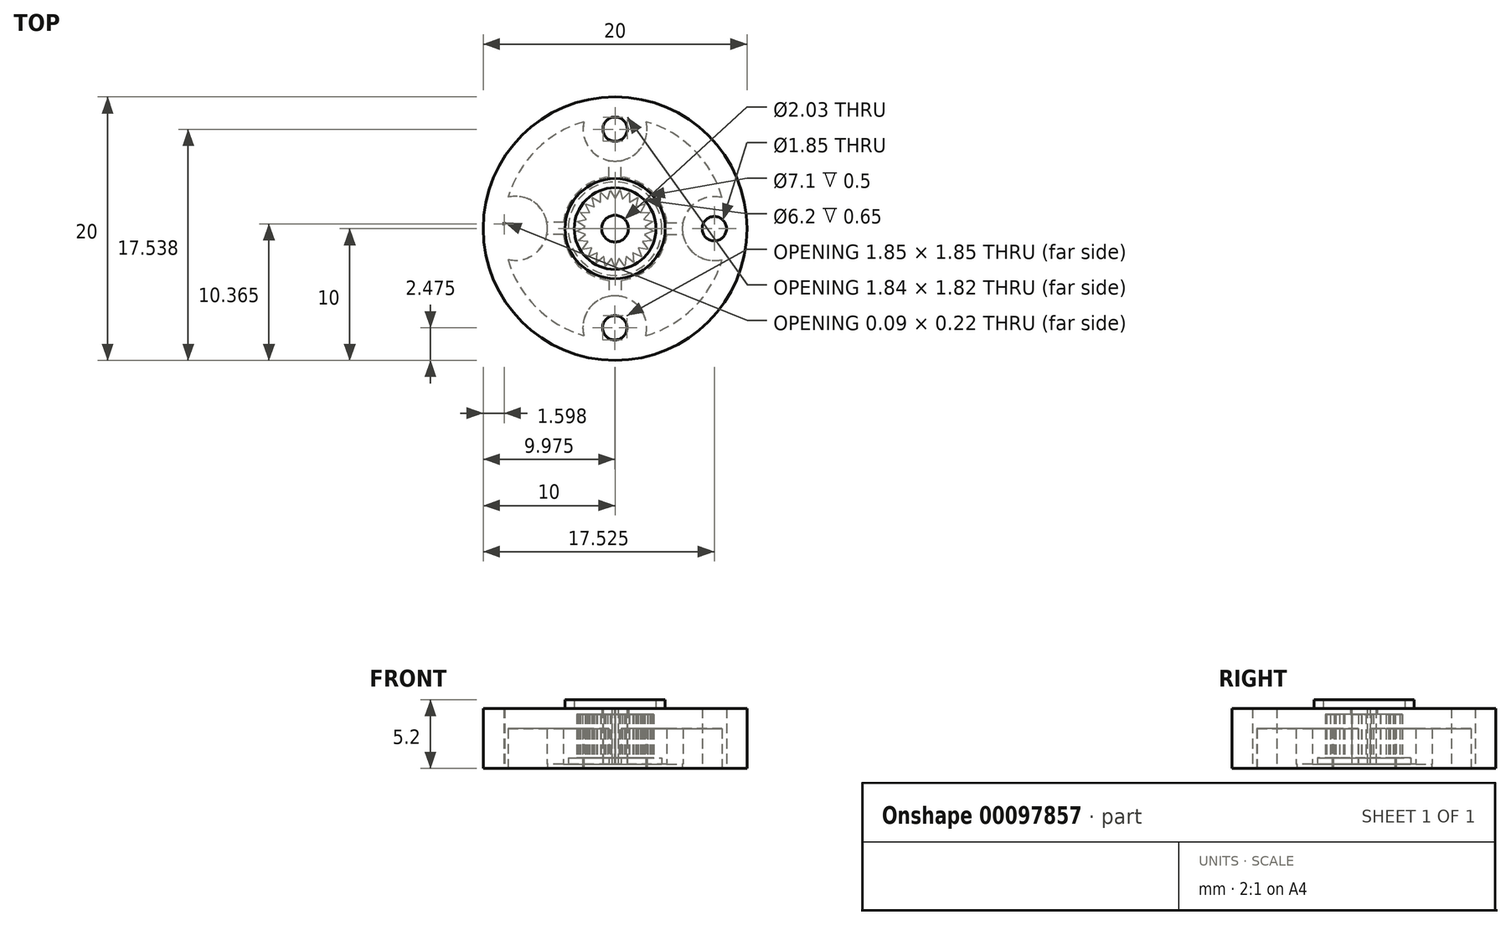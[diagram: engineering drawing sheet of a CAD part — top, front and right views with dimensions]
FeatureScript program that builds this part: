
annotation { "Feature Type Name" : "Feature", "Feature Type Description" : "" }
export const myFeature = defineFeature(function(context is Context, id is Id, definition is map)
    precondition{}
    {
        {
            var Q0;
            Q0=qCreatedBy(makeId("Top.planeOp"),FACE);
            var sketch = newSketch(context, id + "F0", { "sketchPlane" : qUnion([Q0])});
            skCircle(sketch, "E0", {"center": v(0, 0) * mm, "radius": 10 * mm});
            skSolve(sketch);
        }
        {
            var Q0;
            Q0=qSketchRegion(id+"F0",true);
            extrude(context, id + "F1", {"entities" : qUnion([Q0]), "depth" : 4.55 * mm});
        }
        {
            var Q0;
            Q0=makeQuery(id+"F1.opExtrude","CAP_FACE",FACE,{"disambiguationData":[OSD([sQuery(id+"F0.wireOp",EDGE,"E0")])],"isStart":true});
            var sketch = newSketch(context, id + "F2", { "sketchPlane" : qUnion([Q0])});
            skCircle(sketch, "E1", {"center": v(0, 0) * mm, "radius": 8.45 * mm});
            skCircle(sketch, "E2", {"center": v(0, 0) * mm, "radius": 3.95 * mm});
            skCircle(sketch, "E3", {"center": v(0, 0) * mm, "radius": 3.55 * mm});
            skLineSegment(sketch, "E4", {"start": v(0, 8.45) * mm, "end": v(0, -8.45) * mm, "construction": true});
            skLineSegment(sketch, "E5", {"start": v(8.45, 0) * mm, "end": v(-8.45, 0) * mm, "construction": true});
            skLineSegment(sketch, "E6", {"start": v(0.45, 3.92) * mm, "end": v(0.45, 5.15) * mm});
            skLineSegment(sketch, "E7", {"start": v(-0.45, 3.92) * mm, "end": v(-0.45, 5.14) * mm});
            skLineSegment(sketch, "E8", {"start": v(3.92, 0.45) * mm, "end": v(5.14, 0.45) * mm});
            skLineSegment(sketch, "E9", {"start": v(3.92, -0.45) * mm, "end": v(5.14, -0.45) * mm});
            skLineSegment(sketch, "E10", {"start": v(0.45, -3.92) * mm, "end": v(0.45, -5.17) * mm});
            skLineSegment(sketch, "E11", {"start": v(-0.45, -3.92) * mm, "end": v(-0.45, -5.17) * mm});
            skLineSegment(sketch, "E12", {"start": v(-3.92, -0.47) * mm, "end": v(-5.17, -0.47) * mm});
            skLineSegment(sketch, "E13", {"start": v(-3.93, 0.43) * mm, "end": v(-5.17, 0.43) * mm});
            skCircle(sketch, "E14", {"center": v(7.52, 0) * mm, "radius": 0.93 * mm});
            skCircle(sketch, "E15", {"center": v(7.52, 0) * mm, "radius": 2.43 * mm});
            skCircle(sketch, "E16.1.0", {"center": v(-0.02, 7.53) * mm, "radius": 0.93 * mm});
            skCircle(sketch, "E16.1.1", {"center": v(-0.02, 7.53) * mm, "radius": 2.43 * mm});
            skCircle(sketch, "E16.2.0", {"center": v(-7.55, -0.02) * mm, "radius": 0.93 * mm});
            skCircle(sketch, "E16.2.1", {"center": v(-7.55, -0.02) * mm, "radius": 2.43 * mm});
            skCircle(sketch, "E16.3.0", {"center": v(0, -7.55) * mm, "radius": 0.93 * mm});
            skCircle(sketch, "E16.3.1", {"center": v(0, -7.55) * mm, "radius": 2.43 * mm});
            skPoint(sketch, "E16.center", {"position": v(-0.01, -0.01) * mm});
            skLineSegment(sketch, "E17.trimOffspring", {"start": v(8.33, -0.45) * mm, "end": v(8.44, -0.45) * mm});
            skLineSegment(sketch, "E18.trimOffspring", {"start": v(8.33, 0.45) * mm, "end": v(8.44, 0.45) * mm});
            skLineSegment(sketch, "E19.trimOffspring", {"start": v(-0.45, -8.36) * mm, "end": v(-0.45, -8.44) * mm});
            skLineSegment(sketch, "E20.trimOffspring", {"start": v(0.45, -8.36) * mm, "end": v(0.45, -8.44) * mm});
            skLineSegment(sketch, "E21.trimOffspring", {"start": v(-8.36, -0.47) * mm, "end": v(-8.44, -0.47) * mm});
            skLineSegment(sketch, "E22.trimOffspring", {"start": v(-8.36, 0.43) * mm, "end": v(-8.44, 0.43) * mm});
            skLineSegment(sketch, "E23.trimOffspring", {"start": v(-0.45, 8.35) * mm, "end": v(-0.45, 8.44) * mm});
            skLineSegment(sketch, "E24.trimOffspring", {"start": v(0.45, 8.32) * mm, "end": v(0.45, 8.44) * mm});
            skCircle(sketch, "E25", {"center": v(0, 0) * mm, "radius": 1.02 * mm});
            skSolve(sketch);
        }
        {
            var Q0;
            {var subQ1=sQuery(id+"F2.wireOp",EDGE,"E9");Q0=makeQuery(id+"F2.imprint","IMPRINT",FACE,{"disambiguationData":[TD([[makeQuery(id+"F2.imprint","IMPRINT",EDGE,{"derivedFrom":subQ1}),-1.0]])]});}
            var Q1;
            {var subQ0=sQuery(id+"F2.wireOp",EDGE,"E11");Q1=makeQuery(id+"F2.imprint","IMPRINT",FACE,{"disambiguationData":[TD([[makeQuery(id+"F2.imprint","IMPRINT",EDGE,{"derivedFrom":subQ0}),-1.0]])]});}
            var Q2;
            {var subQ0=sQuery(id+"F2.wireOp",EDGE,"E14");var subQ1=makeQuery(id+"F2.imprint","INTERSECT",VERTEX,{"derivedFrom":[subQ0,sQuery(id+"F2.wireOp",EDGE,"E18.trimOffspring")]});Q2=makeQuery(id+"F2.imprint","IMPRINT",FACE,{"disambiguationData":[TD([[makeQuery(id+"F2.imprint","IMPRINT",EDGE,{"disambiguationData":[TD([[subQ1,1.0]])],"derivedFrom":subQ0}),1.0]])]});}
            var Q3;
            {var subQ0=sQuery(id+"F2.wireOp",EDGE,"E16.3.0");var subQ1=sQuery(id+"F2.wireOp",EDGE,"E1");var subQ2=makeQuery(id+"F2.imprint","INTERSECT",VERTEX,{"disambiguationData":[OD(0.0)],"derivedFrom":[subQ1,subQ0]});Q3=makeQuery(id+"F2.imprint","IMPRINT",FACE,{"disambiguationData":[TD([[makeQuery(id+"F2.imprint","IMPRINT",EDGE,{"disambiguationData":[TD([[subQ2,-1.0]])],"derivedFrom":subQ1}),1.0]])]});}
            var Q4;
            {var subQ0=sQuery(id+"F2.wireOp",EDGE,"E16.2.0");var subQ1=sQuery(id+"F2.wireOp",EDGE,"E1");var subQ2=makeQuery(id+"F2.imprint","INTERSECT",VERTEX,{"disambiguationData":[OD(0.0)],"derivedFrom":[subQ1,subQ0]});Q4=makeQuery(id+"F2.imprint","IMPRINT",FACE,{"disambiguationData":[TD([[makeQuery(id+"F2.imprint","IMPRINT",EDGE,{"disambiguationData":[TD([[subQ2,-1.0]])],"derivedFrom":subQ1}),1.0]])]});}
            var Q5;
            {var subQ0=sQuery(id+"F2.wireOp",EDGE,"E7");Q5=makeQuery(id+"F2.imprint","IMPRINT",FACE,{"disambiguationData":[TD([[makeQuery(id+"F2.imprint","IMPRINT",EDGE,{"derivedFrom":subQ0}),1.0]])]});}
            var Q6;
            {var subQ0=sQuery(id+"F2.wireOp",EDGE,"E6");Q6=makeQuery(id+"F2.imprint","IMPRINT",FACE,{"disambiguationData":[TD([[makeQuery(id+"F2.imprint","IMPRINT",EDGE,{"derivedFrom":subQ0}),-1.0]])]});}
            var Q7;
            Q7=makeQuery(id+"F2.imprint","IMPRINT",FACE,{"disambiguationData":[TD([[makeQuery(id+"F2.imprint","IMPRINT",EDGE,{"derivedFrom":sQuery(id+"F2.wireOp",EDGE,"E25")}),1.0]])]});
            var Q8;
            {var subQ0=sQuery(id+"F2.wireOp",EDGE,"E16.1.0");var subQ1=makeQuery(id+"F2.imprint","INTERSECT",VERTEX,{"derivedFrom":[subQ0,sQuery(id+"F2.wireOp",EDGE,"E23.trimOffspring")]});Q8=makeQuery(id+"F2.imprint","IMPRINT",FACE,{"disambiguationData":[TD([[makeQuery(id+"F2.imprint","IMPRINT",EDGE,{"disambiguationData":[TD([[subQ1,-1.0]])],"derivedFrom":subQ0}),1.0]])]});}
            extrude(context, id + "F3", {"entities" : qUnion([Q0, Q1, Q2, Q3, Q4, Q5, Q6, Q7, Q8]), "operationType" : NewBodyOperationType.REMOVE, "oppositeDirection" : true, "depth" : 3 * mm});
        }
        {
            var Q0;
            {var subQ0=sQuery(id+"F2.wireOp",EDGE,"E6");Q0=makeQuery(id+"F2.imprint","IMPRINT",FACE,{"disambiguationData":[TD([[makeQuery(id+"F2.imprint","IMPRINT",EDGE,{"derivedFrom":subQ0}),1.0]])]});}
            var Q1;
            {var subQ0=sQuery(id+"F2.wireOp",EDGE,"E8");Q1=makeQuery(id+"F2.imprint","IMPRINT",FACE,{"disambiguationData":[TD([[makeQuery(id+"F2.imprint","IMPRINT",EDGE,{"derivedFrom":subQ0}),-1.0]])]});}
            var Q2;
            {var subQ0=sQuery(id+"F2.wireOp",EDGE,"E10");Q2=makeQuery(id+"F2.imprint","IMPRINT",FACE,{"disambiguationData":[TD([[makeQuery(id+"F2.imprint","IMPRINT",EDGE,{"derivedFrom":subQ0}),-1.0]])]});}
            var Q3;
            {var subQ0=sQuery(id+"F2.wireOp",EDGE,"E12");Q3=makeQuery(id+"F2.imprint","IMPRINT",FACE,{"disambiguationData":[TD([[makeQuery(id+"F2.imprint","IMPRINT",EDGE,{"derivedFrom":subQ0}),-1.0]])]});}
            var Q4;
            Q4=makeQuery(id+"F2.imprint","IMPRINT",FACE,{"disambiguationData":[TD([[makeQuery(id+"F2.imprint","IMPRINT",EDGE,{"derivedFrom":sQuery(id+"F2.wireOp",EDGE,"E3")}),-1.0]])]});
            extrude(context, id + "F4", {"entities" : qUnion([Q0, Q1, Q2, Q3, Q4]), "operationType" : NewBodyOperationType.REMOVE, "oppositeDirection" : true, "depth" : .3 * mm});
        }
        {
            var Q0;
            Q0=makeQuery(id+"F2.imprint","IMPRINT",FACE,{"disambiguationData":[TD([[makeQuery(id+"F2.imprint","IMPRINT",EDGE,{"derivedFrom":sQuery(id+"F2.wireOp",EDGE,"E3")}),1.0]])]});
            extrude(context, id + "F5", {"entities" : qUnion([Q0]), "operationType" : NewBodyOperationType.REMOVE, "oppositeDirection" : true, "depth" : .8 * mm});
        }
        {
            var Q0;
            Q0=makeQuery(id+"F3.boolean.opBoolean","COPY",FACE,{"derivedFrom":makeQuery(id+"F3.opExtrude","CAP_FACE",FACE,{"disambiguationData":[OSD([sQuery(id+"F2.wireOp",EDGE,"E16.1.0")])],"isStart":false})});
            var Q1;
            Q1=makeQuery(id+"F3.boolean.opBoolean","COPY",FACE,{"derivedFrom":makeQuery(id+"F3.opExtrude","CAP_FACE",FACE,{"disambiguationData":[OSD([sQuery(id+"F2.wireOp",EDGE,"E14")])],"isStart":false})});
            var Q2;
            Q2=makeQuery(id+"F3.boolean.opBoolean","COPY",FACE,{"derivedFrom":makeQuery(id+"F3.opExtrude","CAP_FACE",FACE,{"disambiguationData":[OSD([sQuery(id+"F2.wireOp",EDGE,"E1"),sQuery(id+"F2.wireOp",EDGE,"E16.3.0")])],"isStart":false})});
            var Q3;
            Q3=makeQuery(id+"F3.boolean.opBoolean","COPY",FACE,{"derivedFrom":makeQuery(id+"F3.opExtrude","CAP_FACE",FACE,{"disambiguationData":[OSD([sQuery(id+"F2.wireOp",EDGE,"E25")])],"isStart":false})});
            var Q4;
            Q4=makeQuery(id+"F3.boolean.opBoolean","COPY",FACE,{"derivedFrom":makeQuery(id+"F3.opExtrude","CAP_FACE",FACE,{"disambiguationData":[OSD([sQuery(id+"F2.wireOp",EDGE,"E1"),sQuery(id+"F2.wireOp",EDGE,"E16.2.0")])],"isStart":false})});
            extrude(context, id + "F6", {"entities" : qUnion([Q0, Q1, Q2, Q3, Q4]), "operationType" : NewBodyOperationType.REMOVE, "oppositeDirection" : true, "depth" : 25 * mm});
        }
        {
            var Q0;
            Q0=makeQuery(id+"F5.boolean.opBoolean","COPY",FACE,{"derivedFrom":makeQuery(id+"F5.opExtrude","CAP_FACE",FACE,{"disambiguationData":[OSD([sQuery(id+"F2.wireOp",EDGE,"E3"),sQuery(id+"F2.wireOp",EDGE,"E25")])],"isStart":false})});
            var sketch = newSketch(context, id + "F7", { "sketchPlane" : qUnion([Q0])});
            skCircle(sketch, "E26", {"center": v(0, 0) * mm, "radius": 2.92 * mm});
            skLineSegment(sketch, "E27", {"start": v(0, -2.92) * mm, "end": v(0, 2.92) * mm, "construction": true});
            skCircle(sketch, "E28.cCircle", {"center": v(0, -2.7) * mm, "radius": 0.2 * mm});
            skLineSegment(sketch, "E28.0", {"start": v(-0.36, -2.9) * mm, "end": v(0, -2.28) * mm});
            skLineSegment(sketch, "E28.1", {"start": v(0, -2.28) * mm, "end": v(0.36, -2.9) * mm});
            skLineSegment(sketch, "E28.2", {"start": v(0.36, -2.9) * mm, "end": v(-0.36, -2.9) * mm});
            skPoint(sketch, "E28.0.midPoint", {"position": v(-0.18, -2.6) * mm});
            skLineSegment(sketch, "E29.1.0", {"start": v(0.38, -2.9) * mm, "end": v(0.57, -2.21) * mm});
            skLineSegment(sketch, "E29.1.1", {"start": v(0.57, -2.21) * mm, "end": v(1.07, -2.72) * mm});
            skLineSegment(sketch, "E29.1.2", {"start": v(1.07, -2.72) * mm, "end": v(0.38, -2.9) * mm});
            skLineSegment(sketch, "E29.2.0", {"start": v(1.09, -2.71) * mm, "end": v(1.1, -2) * mm});
            skLineSegment(sketch, "E29.2.1", {"start": v(1.1, -2) * mm, "end": v(1.7, -2.37) * mm});
            skLineSegment(sketch, "E29.2.2", {"start": v(1.7, -2.37) * mm, "end": v(1.09, -2.71) * mm});
            skLineSegment(sketch, "E29.3.0", {"start": v(1.73, -2.36) * mm, "end": v(1.56, -1.66) * mm});
            skLineSegment(sketch, "E29.3.1", {"start": v(1.56, -1.66) * mm, "end": v(2.24, -1.87) * mm});
            skLineSegment(sketch, "E29.3.2", {"start": v(2.24, -1.87) * mm, "end": v(1.73, -2.36) * mm});
            skLineSegment(sketch, "E29.4.0", {"start": v(2.26, -1.85) * mm, "end": v(1.93, -1.22) * mm});
            skLineSegment(sketch, "E29.4.1", {"start": v(1.93, -1.22) * mm, "end": v(2.64, -1.25) * mm});
            skLineSegment(sketch, "E29.4.2", {"start": v(2.64, -1.25) * mm, "end": v(2.26, -1.85) * mm});
            skLineSegment(sketch, "E29.5.0", {"start": v(2.65, -1.23) * mm, "end": v(2.17, -0.7) * mm});
            skLineSegment(sketch, "E29.5.1", {"start": v(2.17, -0.7) * mm, "end": v(2.87, -0.56) * mm});
            skLineSegment(sketch, "E29.5.2", {"start": v(2.87, -0.56) * mm, "end": v(2.65, -1.23) * mm});
            skLineSegment(sketch, "E29.6.0", {"start": v(2.87, -0.54) * mm, "end": v(2.28, -0.14) * mm});
            skLineSegment(sketch, "E29.6.1", {"start": v(2.28, -0.14) * mm, "end": v(2.92, 0.17) * mm});
            skLineSegment(sketch, "E29.6.2", {"start": v(2.92, 0.17) * mm, "end": v(2.87, -0.54) * mm});
            skLineSegment(sketch, "E29.7.0", {"start": v(2.91, 0.2) * mm, "end": v(2.24, 0.43) * mm});
            skLineSegment(sketch, "E29.7.1", {"start": v(2.24, 0.43) * mm, "end": v(2.78, 0.9) * mm});
            skLineSegment(sketch, "E29.7.2", {"start": v(2.78, 0.9) * mm, "end": v(2.91, 0.2) * mm});
            skLineSegment(sketch, "E29.8.0", {"start": v(2.77, 0.91) * mm, "end": v(2.07, 0.97) * mm});
            skLineSegment(sketch, "E29.8.1", {"start": v(2.07, 0.97) * mm, "end": v(2.47, 1.56) * mm});
            skLineSegment(sketch, "E29.8.2", {"start": v(2.47, 1.56) * mm, "end": v(2.77, 0.91) * mm});
            skLineSegment(sketch, "E29.9.0", {"start": v(2.46, 1.57) * mm, "end": v(1.76, 1.46) * mm});
            skLineSegment(sketch, "E29.9.1", {"start": v(1.76, 1.46) * mm, "end": v(2, 2.12) * mm});
            skLineSegment(sketch, "E29.9.2", {"start": v(2, 2.12) * mm, "end": v(2.46, 1.57) * mm});
            skLineSegment(sketch, "E29.10.0", {"start": v(2, 2.14) * mm, "end": v(1.34, 1.85) * mm});
            skLineSegment(sketch, "E29.10.1", {"start": v(1.34, 1.85) * mm, "end": v(1.42, 2.55) * mm});
            skLineSegment(sketch, "E29.10.2", {"start": v(1.42, 2.55) * mm, "end": v(2, 2.14) * mm});
            skLineSegment(sketch, "E29.11.0", {"start": v(1.4, 2.56) * mm, "end": v(0.84, 2.12) * mm});
            skLineSegment(sketch, "E29.11.1", {"start": v(0.84, 2.12) * mm, "end": v(0.74, 2.83) * mm});
            skLineSegment(sketch, "E29.11.2", {"start": v(0.74, 2.83) * mm, "end": v(1.4, 2.56) * mm});
            skLineSegment(sketch, "E29.12.0", {"start": v(0.72, 2.83) * mm, "end": v(0.29, 2.27) * mm});
            skLineSegment(sketch, "E29.12.1", {"start": v(0.29, 2.27) * mm, "end": v(0.01, 2.92) * mm});
            skLineSegment(sketch, "E29.12.2", {"start": v(0.01, 2.92) * mm, "end": v(0.72, 2.83) * mm});
            skLineSegment(sketch, "E29.13.0", {"start": v(-0.01, 2.92) * mm, "end": v(-0.29, 2.27) * mm});
            skLineSegment(sketch, "E29.13.1", {"start": v(-0.29, 2.27) * mm, "end": v(-0.72, 2.83) * mm});
            skLineSegment(sketch, "E29.13.2", {"start": v(-0.72, 2.83) * mm, "end": v(-0.01, 2.92) * mm});
            skLineSegment(sketch, "E29.14.0", {"start": v(-0.74, 2.83) * mm, "end": v(-0.84, 2.12) * mm});
            skLineSegment(sketch, "E29.14.1", {"start": v(-0.84, 2.12) * mm, "end": v(-1.4, 2.56) * mm});
            skLineSegment(sketch, "E29.14.2", {"start": v(-1.4, 2.56) * mm, "end": v(-0.74, 2.83) * mm});
            skLineSegment(sketch, "E29.15.0", {"start": v(-1.42, 2.55) * mm, "end": v(-1.34, 1.85) * mm});
            skLineSegment(sketch, "E29.15.1", {"start": v(-1.34, 1.85) * mm, "end": v(-2, 2.14) * mm});
            skLineSegment(sketch, "E29.15.2", {"start": v(-2, 2.14) * mm, "end": v(-1.42, 2.55) * mm});
            skLineSegment(sketch, "E29.16.0", {"start": v(-2, 2.12) * mm, "end": v(-1.76, 1.46) * mm});
            skLineSegment(sketch, "E29.16.1", {"start": v(-1.76, 1.46) * mm, "end": v(-2.46, 1.57) * mm});
            skLineSegment(sketch, "E29.16.2", {"start": v(-2.46, 1.57) * mm, "end": v(-2, 2.12) * mm});
            skLineSegment(sketch, "E29.17.0", {"start": v(-2.47, 1.56) * mm, "end": v(-2.07, 0.97) * mm});
            skLineSegment(sketch, "E29.17.1", {"start": v(-2.07, 0.97) * mm, "end": v(-2.77, 0.91) * mm});
            skLineSegment(sketch, "E29.17.2", {"start": v(-2.77, 0.91) * mm, "end": v(-2.47, 1.56) * mm});
            skLineSegment(sketch, "E29.18.0", {"start": v(-2.78, 0.9) * mm, "end": v(-2.24, 0.43) * mm});
            skLineSegment(sketch, "E29.18.1", {"start": v(-2.24, 0.43) * mm, "end": v(-2.91, 0.2) * mm});
            skLineSegment(sketch, "E29.18.2", {"start": v(-2.91, 0.2) * mm, "end": v(-2.78, 0.9) * mm});
            skLineSegment(sketch, "E29.19.0", {"start": v(-2.92, 0.17) * mm, "end": v(-2.28, -0.14) * mm});
            skLineSegment(sketch, "E29.19.1", {"start": v(-2.28, -0.14) * mm, "end": v(-2.87, -0.54) * mm});
            skLineSegment(sketch, "E29.19.2", {"start": v(-2.87, -0.54) * mm, "end": v(-2.92, 0.17) * mm});
            skLineSegment(sketch, "E29.20.0", {"start": v(-2.87, -0.56) * mm, "end": v(-2.17, -0.7) * mm});
            skLineSegment(sketch, "E29.20.1", {"start": v(-2.17, -0.7) * mm, "end": v(-2.65, -1.23) * mm});
            skLineSegment(sketch, "E29.20.2", {"start": v(-2.65, -1.23) * mm, "end": v(-2.87, -0.56) * mm});
            skLineSegment(sketch, "E29.21.0", {"start": v(-2.64, -1.25) * mm, "end": v(-1.93, -1.22) * mm});
            skLineSegment(sketch, "E29.21.1", {"start": v(-1.93, -1.22) * mm, "end": v(-2.26, -1.85) * mm});
            skLineSegment(sketch, "E29.21.2", {"start": v(-2.26, -1.85) * mm, "end": v(-2.64, -1.25) * mm});
            skLineSegment(sketch, "E29.22.0", {"start": v(-2.24, -1.87) * mm, "end": v(-1.56, -1.66) * mm});
            skLineSegment(sketch, "E29.22.1", {"start": v(-1.56, -1.66) * mm, "end": v(-1.73, -2.36) * mm});
            skLineSegment(sketch, "E29.22.2", {"start": v(-1.73, -2.36) * mm, "end": v(-2.24, -1.87) * mm});
            skLineSegment(sketch, "E29.23.0", {"start": v(-1.7, -2.37) * mm, "end": v(-1.1, -2) * mm});
            skLineSegment(sketch, "E29.23.1", {"start": v(-1.1, -2) * mm, "end": v(-1.09, -2.71) * mm});
            skLineSegment(sketch, "E29.23.2", {"start": v(-1.09, -2.71) * mm, "end": v(-1.7, -2.37) * mm});
            skLineSegment(sketch, "E29.24.0", {"start": v(-1.07, -2.72) * mm, "end": v(-0.57, -2.21) * mm});
            skLineSegment(sketch, "E29.24.1", {"start": v(-0.57, -2.21) * mm, "end": v(-0.38, -2.9) * mm});
            skLineSegment(sketch, "E29.24.2", {"start": v(-0.38, -2.9) * mm, "end": v(-1.07, -2.72) * mm});
            skSolve(sketch);
        }
        {
            var Q0;
            {var subQ50=sQuery(id+"F7.wireOp",EDGE,"E29.1.0");Q0=makeQuery(id+"F7.imprint","IMPRINT",FACE,{"disambiguationData":[TD([[makeQuery(id+"F7.imprint","IMPRINT",EDGE,{"derivedFrom":subQ50}),1.0]])]});}
            extrude(context, id + "F8", {"entities" : qUnion([Q0]), "operationType" : NewBodyOperationType.REMOVE, "oppositeDirection" : true, "depth" : 3.3 * mm});
        }
        {
            var Q0;
            Q0=makeQuery(id+"F1.opExtrude","CAP_FACE",FACE,{"disambiguationData":[OSD([sQuery(id+"F0.wireOp",EDGE,"E0")])],"isStart":false});
            var sketch = newSketch(context, id + "F9", { "sketchPlane" : qUnion([Q0])});
            skCircle(sketch, "E30", {"center": v(0, 0) * mm, "radius": 3.8 * mm});
            skCircle(sketch, "E31", {"center": v(0, 0) * mm, "radius": 3.1 * mm});
            skSolve(sketch);
        }
        {
            var Q0;
            Q0=makeQuery(id+"F9.imprint","IMPRINT",FACE,{"disambiguationData":[TD([[makeQuery(id+"F9.imprint","IMPRINT",EDGE,{"derivedFrom":sQuery(id+"F9.wireOp",EDGE,"E30")}),1.0]])]});
            extrude(context, id + "F10", {"entities" : qUnion([Q0]), "operationType" : NewBodyOperationType.ADD, "depth" : .65 * mm});
        }
    });
